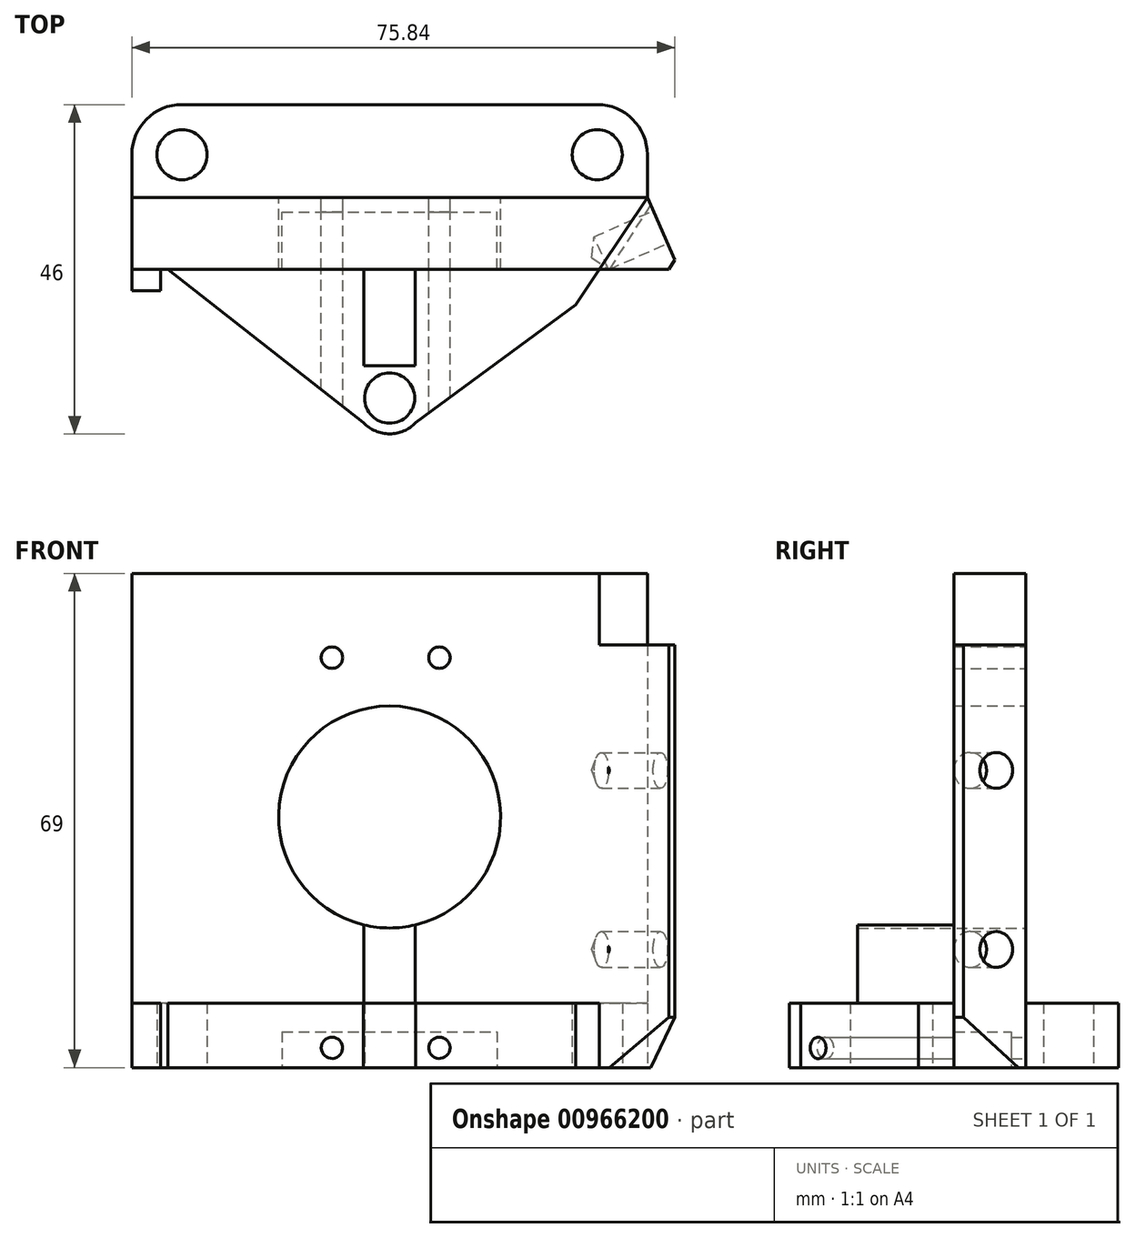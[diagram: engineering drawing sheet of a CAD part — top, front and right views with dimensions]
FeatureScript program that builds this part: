
annotation { "Feature Type Name" : "Feature", "Feature Type Description" : "" }
export const myFeature = defineFeature(function(context is Context, id is Id, definition is map)
    precondition{}
    {
        {
            var Q0;
            Q0=qCreatedBy(makeId("Top.planeOp"),FACE);
            var sketch = newSketch(context, id + "F0", { "sketchPlane" : qUnion([Q0])});
            skLineSegment(sketch, "E0", {"start": v(-36, -26) * mm, "end": v(-32, -26) * mm});
            skLineSegment(sketch, "E1", {"start": v(-32, -26) * mm, "end": v(-32, -23) * mm});
            skLineSegment(sketch, "E2", {"start": v(-32, -23) * mm, "end": v(-31, -23) * mm});
            skLineSegment(sketch, "E3", {"start": v(-31, -23) * mm, "end": v(-3.64, -44.43) * mm});
            skLineSegment(sketch, "E4", {"start": v(-29, 0) * mm, "end": v(29, 0) * mm});
            skLineSegment(sketch, "E5", {"start": v(-36, -26) * mm, "end": v(-36, -7) * mm});
            skCircle(sketch, "E6", {"center": v(-29, -7) * mm, "radius": 3.5 * mm});
            skCircle(sketch, "E7", {"center": v(29, -7) * mm, "radius": 3.5 * mm});
            skCircle(sketch, "E8", {"center": v(0, -41) * mm, "radius": 3.5 * mm});
            skArc(sketch, "E9", {"start": v(-3.64, -44.43) * mm, "mid": v(0, -46) * mm, "end": v(3.64, -44.43) * mm});
            skArc(sketch, "E10", {"start": v(-36, -7) * mm, "mid": v(-33.95, -2.05) * mm, "end": v(-29, 0) * mm});
            skArc(sketch, "E11", {"start": v(29, 0) * mm, "mid": v(33.95, -2.05) * mm, "end": v(36, -7) * mm});
            skLineSegment(sketch, "E12", {"start": v(26, -27.97) * mm, "end": v(3.64, -44.43) * mm});
            skLineSegment(sketch, "E13", {"start": v(26, -27.97) * mm, "end": v(36, -13) * mm});
            skLineSegment(sketch, "E14", {"start": v(36, -13) * mm, "end": v(36, -7) * mm});
            skSolve(sketch);
        }
        {
            var Q0;
            Q0=qSketchRegion(id+"F0",true);
            extrude(context, id + "F1", {"entities" : qUnion([Q0]), "depth" : 9 * mm});
        }
        {
            var Q0;
            Q0=makeQuery(id+"F0.imprint","IMPRINT",FACE,{"disambiguationData":[TD([[makeQuery(id+"F0.imprint","IMPRINT",EDGE,{"derivedFrom":sQuery(id+"F0.wireOp",EDGE,"E0")}),1.0]])]});
            var sketch = newSketch(context, id + "F2", { "sketchPlane" : qUnion([Q0])});
            skLineSegment(sketch, "E15.bottom", {"start": v(-15, -23) * mm, "end": v(15, -23) * mm});
            skLineSegment(sketch, "E15.top", {"start": v(-15, -15) * mm, "end": v(15, -15) * mm});
            skLineSegment(sketch, "E15.left", {"start": v(-15, -23) * mm, "end": v(-15, -15) * mm});
            skLineSegment(sketch, "E15.right", {"start": v(15, -23) * mm, "end": v(15, -15) * mm});
            skPoint(sketch, "E15.middle", {"position": v(0, -19) * mm});
            skSolve(sketch);
        }
        {
            var Q0;
            Q0=qSketchRegion(id+"F2",true);
            extrude(context, id + "F3", {"entities" : qUnion([Q0]), "operationType" : NewBodyOperationType.REMOVE, "depth" : 5 * mm});
        }
        {
            var Q0;
            Q0=makeQuery(id+"F1.opExtrude","CAP_FACE",FACE,{"disambiguationData":[OSD([sQuery(id+"F0.wireOp",EDGE,"E0"),sQuery(id+"F0.wireOp",EDGE,"E1"),sQuery(id+"F0.wireOp",EDGE,"E2"),sQuery(id+"F0.wireOp",EDGE,"E3"),sQuery(id+"F0.wireOp",EDGE,"E4"),sQuery(id+"F0.wireOp",EDGE,"E5"),sQuery(id+"F0.wireOp",EDGE,"E6"),sQuery(id+"F0.wireOp",EDGE,"E7"),sQuery(id+"F0.wireOp",EDGE,"E8"),sQuery(id+"F0.wireOp",EDGE,"E9"),sQuery(id+"F0.wireOp",EDGE,"E10"),sQuery(id+"F0.wireOp",EDGE,"E11"),sQuery(id+"F0.wireOp",EDGE,"WJA2m645-39Qq-lADn-E0cL-840yLO94TB4h"),sQuery(id+"F0.wireOp",EDGE,"E12")])],"isStart":false});
            var sketch = newSketch(context, id + "F4", { "sketchPlane" : qUnion([Q0])});
            skPoint(sketch, "E16.middle.positionSnap0", {"position": v(0, 0) * mm});
            skPoint(sketch, "E16.centerSnap0", {"position": v(0, 0) * mm});
            skLineSegment(sketch, "E17", {"start": v(-36, -13) * mm, "end": v(36, -13) * mm});
            skLineSegment(sketch, "E18", {"start": v(36, -13) * mm, "end": v(39.84, -21.7) * mm});
            skLineSegment(sketch, "E19", {"start": v(39.84, -21.7) * mm, "end": v(39, -23) * mm});
            skLineSegment(sketch, "E20", {"start": v(39, -23) * mm, "end": v(-36, -23) * mm});
            skLineSegment(sketch, "E21", {"start": v(-36, -13) * mm, "end": v(-36, -23) * mm});
            skSolve(sketch);
        }
        {
            var Q0;
            {var subQ7=sQuery(id+"F4.wireOp",EDGE,"E17");Q0=makeQuery(id+"F4.imprint","IMPRINT",FACE,{"disambiguationData":[TD([[makeQuery(id+"F4.imprint","IMPRINT",EDGE,{"derivedFrom":subQ7}),-1.0]])]});}
            var Q1;
            {var subQ0=sQuery(id+"F4.wireOp",EDGE,"E21");Q1=makeQuery(id+"F4.imprint","IMPRINT",FACE,{"disambiguationData":[TD([[makeQuery(id+"F4.imprint","IMPRINT",EDGE,{"derivedFrom":subQ0}),-1.0]])]});}
            extrude(context, id + "F5", {"entities" : qUnion([Q0, Q1]), "operationType" : NewBodyOperationType.ADD, "depth" : 60 * mm});
        }
        {
            var Q0;
            {var subQ3=sQuery(id+"F4.wireOp",EDGE,"E18");Q0=makeQuery(id+"F4.imprint","IMPRINT",FACE,{"disambiguationData":[TD([[makeQuery(id+"F4.imprint","IMPRINT",EDGE,{"derivedFrom":subQ3}),-1.0]])]});}
            extrude(context, id + "F6", {"entities" : qUnion([Q0]), "operationType" : NewBodyOperationType.ADD, "depth" : 50 * mm});
        }
        {
            var Q0;
            {var subQ3=sQuery(id+"F4.wireOp",EDGE,"E18");Q0=makeQuery(id+"F4.imprint","IMPRINT",FACE,{"disambiguationData":[TD([[makeQuery(id+"F4.imprint","IMPRINT",EDGE,{"derivedFrom":subQ3}),-1.0]])]});}
            extrude(context, id + "F7", {"entities" : qUnion([Q0]), "operationType" : NewBodyOperationType.ADD, "oppositeDirection" : true, "depth" : 9 * mm});
        }
        {
            var Q0;
            Q0=makeQuery(id+"F7.opExtrude","CAP_EDGE",EDGE,{"disambiguationData":[OSD([sQuery(id+"F4.wireOp",EDGE,"E19")])],"isStart":false});
            chamfer(context, id + "F8", {"entities" : qUnion([Q0]), "width" : 7 * mm, "tangentPropagation" : true});
        }
        {
            var Q0;
            {var subQ0=sQuery(id+"F4.wireOp",EDGE,"E18");Q0=makeQuery(id+"F7.boolean.opBoolean","MERGE",FACE,{"derivedFrom":[makeQuery(id+"F6.opExtrude","SWEPT_FACE",FACE,{"disambiguationData":[OSD([subQ0])]}),makeQuery(id+"F7.opExtrude","SWEPT_FACE",FACE,{"disambiguationData":[OSD([subQ0])]})]});}
            var sketch = newSketch(context, id + "F9", { "sketchPlane" : qUnion([Q0])});
            skPoint(sketch, "E22", {"position": v(-30.93, 41.5) * mm});
            skPoint(sketch, "E23", {"position": v(-30.93, 16.5) * mm});
            skSolve(sketch);
        }
        {
            var Q0;
            Q0=sQuery(id+"F9.wireOp",VERTEX,"E23");
            var Q1;
            Q1=sQuery(id+"F9.wireOp",VERTEX,"E22");
            var Q2;
            Q2=makeQuery(id+"F1.opExtrude","SWEPT_BODY",BODY,{"disambiguationData":[OSD([sQuery(id+"F0.wireOp",EDGE,"E0"),sQuery(id+"F0.wireOp",EDGE,"E1"),sQuery(id+"F0.wireOp",EDGE,"E2"),sQuery(id+"F0.wireOp",EDGE,"E3"),sQuery(id+"F0.wireOp",EDGE,"E4"),sQuery(id+"F0.wireOp",EDGE,"E5"),sQuery(id+"F0.wireOp",EDGE,"E6"),sQuery(id+"F0.wireOp",EDGE,"E7"),sQuery(id+"F0.wireOp",EDGE,"E8"),sQuery(id+"F0.wireOp",EDGE,"E9"),sQuery(id+"F0.wireOp",EDGE,"E10"),sQuery(id+"F0.wireOp",EDGE,"E11"),sQuery(id+"F0.wireOp",EDGE,"E12"),sQuery(id+"F0.wireOp",EDGE,"E13"),sQuery(id+"F0.wireOp",EDGE,"E14")])]});
            hole(context, id + "F10", {"style" : HoleStyle.SIMPLE, "endStyle" : HoleEndStyle.BLIND, "holeDiameter" : 5 * mm, "holeDepth" : 9 * mm, "tappedDepth" : 12 * mm, "tapClearance" : 3, "startFromSketch" : true, "locations" : qUnion([Q0, Q1]), "scope" : qUnion([Q2])});
        }
        {
            var Q0;
            {var subQ0=sQuery(id+"F0.wireOp",EDGE,"E9");var subQ1=sQuery(id+"F0.wireOp",EDGE,"E8");var subQ2=sQuery(id+"F0.wireOp",EDGE,"E3");var subQ3=sQuery(id+"F0.wireOp",EDGE,"E2");var subQ4=sQuery(id+"F0.wireOp",EDGE,"E13");var subQ5=sQuery(id+"F0.wireOp",EDGE,"E12");Q0=makeQuery(id+"F5.boolean.opBoolean","SPLIT",FACE,{"disambiguationData":[TD([makeQuery(id+"F1.opExtrude","SWEPT_FACE",FACE,{"disambiguationData":[OSD([subQ2])]})])],"derivedFrom":makeQuery(id+"F1.opExtrude","CAP_FACE",FACE,{"disambiguationData":[OSD([sQuery(id+"F0.wireOp",EDGE,"E0"),sQuery(id+"F0.wireOp",EDGE,"E1"),subQ3,subQ2,sQuery(id+"F0.wireOp",EDGE,"E4"),sQuery(id+"F0.wireOp",EDGE,"E5"),sQuery(id+"F0.wireOp",EDGE,"E6"),sQuery(id+"F0.wireOp",EDGE,"E7"),subQ1,subQ0,sQuery(id+"F0.wireOp",EDGE,"E10"),sQuery(id+"F0.wireOp",EDGE,"E11"),subQ5,subQ4,sQuery(id+"F0.wireOp",EDGE,"E14")])],"isStart":false})});}
            var sketch = newSketch(context, id + "F11", { "sketchPlane" : qUnion([Q0])});
            skLineSegment(sketch, "E24.bottom", {"start": v(3.6, -36.46) * mm, "end": v(-3.6, -36.46) * mm});
            skLineSegment(sketch, "E24.top", {"start": v(3.6, -19.46) * mm, "end": v(-3.6, -19.46) * mm});
            skLineSegment(sketch, "E24.left", {"start": v(3.6, -36.46) * mm, "end": v(3.6, -19.46) * mm});
            skLineSegment(sketch, "E24.right", {"start": v(-3.6, -36.46) * mm, "end": v(-3.6, -19.46) * mm});
            skPoint(sketch, "E24.middle", {"position": v(0, -27.96) * mm});
            skSolve(sketch);
        }
        {
            var Q0;
            Q0=qSketchRegion(id+"F11",true);
            extrude(context, id + "F12", {"entities" : qUnion([Q0]), "operationType" : NewBodyOperationType.ADD, "depth" : 25 * mm});
        }
        {
            var Q0;
            Q0=makeQuery(id+"F5.opExtrude","SWEPT_FACE",FACE,{"disambiguationData":[OSD([sQuery(id+"F4.wireOp",EDGE,"E17")])]});
            var sketch = newSketch(context, id + "F13", { "sketchPlane" : qUnion([Q0])});
            skCircle(sketch, "E25", {"center": v(-6.95, 2.75) * mm, "radius": 1.5 * mm});
            skCircle(sketch, "E26", {"center": v(-6.95, 57.25) * mm, "radius": 1.5 * mm});
            skCircle(sketch, "E27", {"center": v(8.05, 57.25) * mm, "radius": 1.5 * mm});
            skCircle(sketch, "E28", {"center": v(8.05, 2.75) * mm, "radius": 1.5 * mm});
            skLineSegment(sketch, "E29.bottom", {"start": v(-9.7, 0) * mm, "end": v(-9.7, 60) * mm});
            skLineSegment(sketch, "E29.top", {"start": v(10.8, 0) * mm, "end": v(10.8, 60) * mm});
            skLineSegment(sketch, "E29.left", {"start": v(-9.7, 0) * mm, "end": v(10.8, 0) * mm});
            skLineSegment(sketch, "E29.right", {"start": v(-9.7, 60) * mm, "end": v(10.8, 60) * mm});
            skSolve(sketch);
        }
        {
            var Q0;
            Q0=makeQuery(id+"F13.imprint","IMPRINT",FACE,{"disambiguationData":[TD([[makeQuery(id+"F13.imprint","IMPRINT",EDGE,{"derivedFrom":sQuery(id+"F13.wireOp",EDGE,"E25")}),1.0]])]});
            var Q1;
            Q1=makeQuery(id+"F13.imprint","IMPRINT",FACE,{"disambiguationData":[TD([[makeQuery(id+"F13.imprint","IMPRINT",EDGE,{"derivedFrom":sQuery(id+"F13.wireOp",EDGE,"E28")}),1.0]])]});
            var Q2;
            Q2=makeQuery(id+"F13.imprint","IMPRINT",FACE,{"disambiguationData":[TD([[makeQuery(id+"F13.imprint","IMPRINT",EDGE,{"derivedFrom":sQuery(id+"F13.wireOp",EDGE,"E27")}),1.0]])]});
            var Q3;
            Q3=makeQuery(id+"F13.imprint","IMPRINT",FACE,{"disambiguationData":[TD([[makeQuery(id+"F13.imprint","IMPRINT",EDGE,{"derivedFrom":sQuery(id+"F13.wireOp",EDGE,"E26")}),1.0]])]});
            extrude(context, id + "F14", {"entities" : qUnion([Q0, Q1, Q2, Q3]), "operationType" : NewBodyOperationType.REMOVE, "endBound" : BoundingType.THROUGH_ALL, "oppositeDirection" : true, "depth" : 25 * mm});
        }
        {
            var Q0;
            {var subQ0=sQuery(id+"F0.wireOp",EDGE,"E10");var subQ1=sQuery(id+"F0.wireOp",EDGE,"E14");var subQ2=sQuery(id+"F0.wireOp",EDGE,"E13");var subQ3=sQuery(id+"F0.wireOp",EDGE,"E11");var subQ4=sQuery(id+"F0.wireOp",EDGE,"E4");var subQ5=sQuery(id+"F0.wireOp",EDGE,"E5");var subQ6=sQuery(id+"F0.wireOp",EDGE,"E6");var subQ7=sQuery(id+"F0.wireOp",EDGE,"E7");Q0=makeQuery(id+"F5.boolean.opBoolean","SPLIT",FACE,{"disambiguationData":[TD([makeQuery(id+"F1.opExtrude","SWEPT_FACE",FACE,{"disambiguationData":[OSD([subQ4])]})])],"derivedFrom":makeQuery(id+"F1.opExtrude","CAP_FACE",FACE,{"disambiguationData":[OSD([sQuery(id+"F0.wireOp",EDGE,"E0"),sQuery(id+"F0.wireOp",EDGE,"E1"),sQuery(id+"F0.wireOp",EDGE,"E2"),sQuery(id+"F0.wireOp",EDGE,"E3"),subQ4,subQ5,subQ6,subQ7,sQuery(id+"F0.wireOp",EDGE,"E8"),sQuery(id+"F0.wireOp",EDGE,"E9"),subQ0,subQ3,sQuery(id+"F0.wireOp",EDGE,"E12"),subQ2,subQ1])],"isStart":false})});}
            var sketch = newSketch(context, id + "F15", { "sketchPlane" : qUnion([Q0])});
            skSolve(sketch);
        }
        {
            var Q0;
            Q0=makeQuery(id+"FEbFz6zTrpfMZsp_1.boolean.opBoolean","MERGE",FACE,{"derivedFrom":[makeQuery(id+"F5.opExtrude","SWEPT_FACE",FACE,{"disambiguationData":[OSD([sQuery(id+"F4.wireOp",EDGE,"E17")])]}),makeQuery(id+"FEbFz6zTrpfMZsp_1.opExtrude","SWEPT_FACE",FACE,{"disambiguationData":[OSD([sQuery(id+"F15.wireOp",EDGE,"UuulbaJ0-uh5O-iian-63B3-8MHiHCaYlGRc.top")])]})]});
            var sketch = newSketch(context, id + "F16", { "sketchPlane" : qUnion([Q0])});
            skCircle(sketch, "E30", {"center": v(0, 35) * mm, "radius": 15.5 * mm});
            skSolve(sketch);
        }
        {
            var Q0;
            Q0=qSketchRegion(id+"F16",true);
            extrude(context, id + "F17", {"entities" : qUnion([Q0]), "operationType" : NewBodyOperationType.REMOVE, "oppositeDirection" : true, "depth" : 25 * mm});
        }
    });
